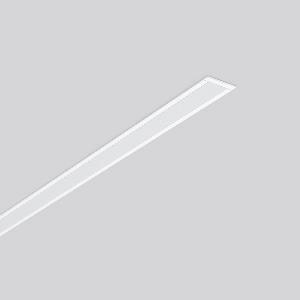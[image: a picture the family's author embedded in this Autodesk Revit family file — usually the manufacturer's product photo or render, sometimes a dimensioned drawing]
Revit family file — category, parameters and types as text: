
# Revit family: less_is_more_27_312178_002_76_eb57
name_source: partatom
category: Lighting Fixtures
units: mm (PartAtom-declared; Revit-internal decimal feet)

## family parameters
Cut with Voids When Loaded = No
Host = Face
Light Source = No
Part Type = Normal
Room Calculation Point = No
Round Connector Dimension = Use Diameter
Shared = No

## types (1)
- LESS IS MORE 27 (1 x LED Modul 830, 2900 lm, 3000)
    Apparent Load = 43 VA
    CIE Flux Codes = 48 79 96 100 100
    Color Rendering = 80
    Color Temperature = 3000
    Default Elevation = 1800 mm
    Description = Series: LESS IS MORE 27
Recessed ceiling and wall luminaire with slim design. Housing: extruded aluminium profile, powder-coated. End cap aluminium powder-coated. Diffuser made of non-yellowing plastic (PMMA), opal. Suitable for Recessed ceiling mounting, wall (recessed). External driver with connecting cable. 
Colour: traffic white, matt (RAL 9016)
Length: 1514 mm
Width: 38 mm
Height: 2 mm
Cut-out length: 1506 mm
Cut-out width: 30 mm
Recess height: 45-60 mm
Luminaire: recess height: 37 mm
Lamp: LED
Socket: without socket
Colour temperature: 3000K
Colour rendering index (CRI): 82
System power: 43 W
Rated luminous flux: 2900 lm
Luminous efficiency: 67 lm/W
Control gear: Voltage converter, DALI dim.
Protection class: II
Type of protection: IP 20
    Height = 0 mm  [stored 0 ft]
    Lamp = 1 x LED Modul 830
    Lamp Light Flux = 2900 lm
    Lamp count = 1
    Length = 1514 mm
    Lifetime = 50000 h
    Luminous efficacy = 67 lm/W
    Manufacturer = RZB
    ModVariant = No
    Model = 312178.002.76
    Mounting Place = Ceiling, Wall
    Mounting Type = Recessed
    Number of Poles = 1
    OnlyDefault = Yes
    Power Factor = 1
    Product Name = LESS IS MORE 27
    Product group = Recessed LED linear luminaires
    ProductGroupID = 407
    Protection Class = Protection class II
    Protection Degree = IP 20
    RLX_Detail_Level = 1
    RLX_Emergency_Light_Flux = 0 lm
    RLX_Emergency_Type = 0
    RLX_Emergency_Type_DB = No
    RlxData = <blob elided: 21629 chars, md5=49b17941>
    Socket = socket
    Standby Power = 0 W
    System Light Flux = 2900 lm
    System Power = 43 W
    Type Comments = Product without accessories
    Type Image = 312176.002.jpg
    URL = http://relux.com
    VarID = ---
    Voltage = 230 V
    Voltage Range = 220-240 V
    Weight = 0.00 kg
    Width = 38 mm

note: [stored X ft] marks values corroborated as IEEE doubles in the binary element streams (Revit-internal decimal feet)

## geometry (parser evidence)
native form markers: Blend x4, Sweep x12
no freeform markers — native parametric forms only
